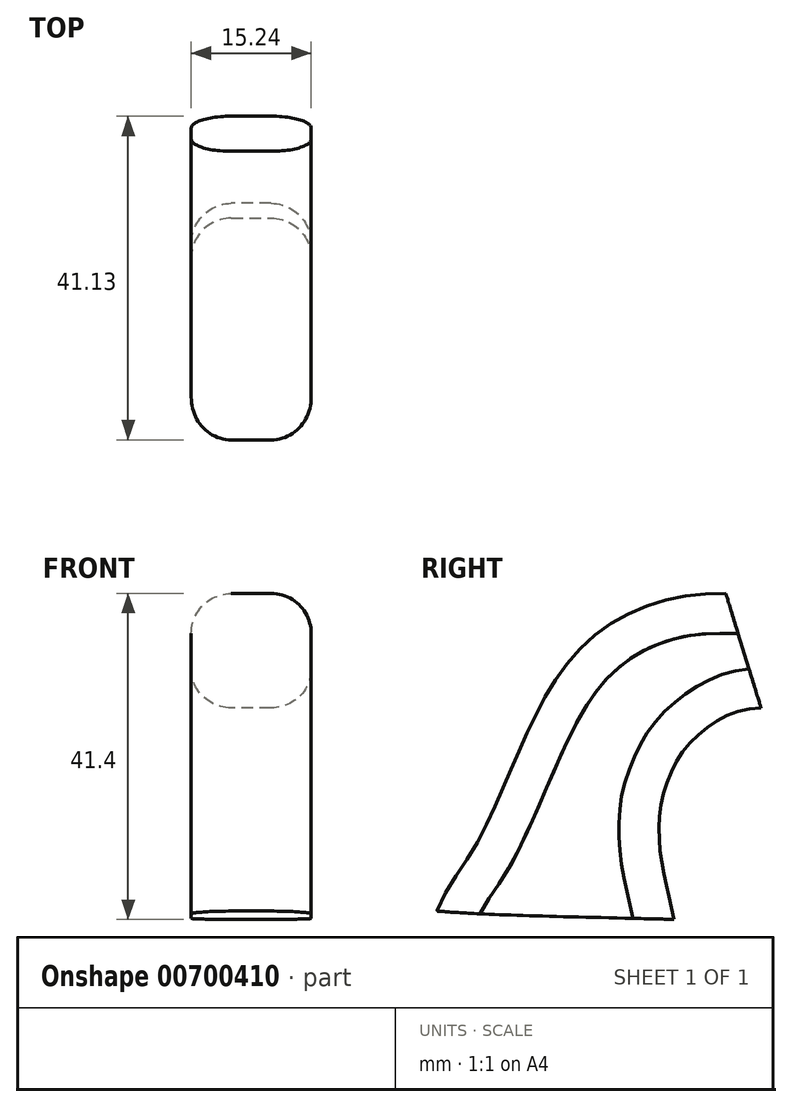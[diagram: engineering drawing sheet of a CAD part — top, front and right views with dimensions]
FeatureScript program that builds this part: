
annotation { "Feature Type Name" : "Feature", "Feature Type Description" : "" }
export const myFeature = defineFeature(function(context is Context, id is Id, definition is map)
    precondition{}
    {
        {
            var Q0;
            Q0=qCreatedBy(makeId("Right.planeOp"),FACE);
            var sketch = newSketch(context, id + "F0", { "sketchPlane" : qUnion([Q0])});
            skLineSegment(sketch, "E0", {"start": v(37.28, 25.36) * mm, "end": v(105.89, 25.36) * mm});
            skFitSpline(sketch, "E1", {"points": [v(-10.84, 4.07) * mm, v(-16.36, 3.73) * mm, v(-23.37, 1.43) * mm, v(-29.24, -2.83) * mm, v(-34.98, -11.33) * mm, v(-42.45, -27.65) * mm, v(-45.67, -32.6) * mm, v(-47.51, -36.27) * mm], "startDerivative": vector(-44.57, -0.2) * mm, "endDerivative": vector(-16.28, -36.6) * mm});
            skFitSpline(sketch, "E2", {"points": [v(-47.51, -36.27) * mm, v(-41.71, -36.64) * mm, v(-17.45, -37.32) * mm], "startDerivative": vector(14.62, -1.12) * mm, "endDerivative": vector(42.34, -0.99) * mm});
            skFitSpline(sketch, "E3", {"points": [v(-17.45, -37.32) * mm, v(-18.37, -32.95) * mm, v(-19.2, -28.6) * mm, v(-19.05, -22.42) * mm, v(-18, -19.24) * mm, v(-16.6, -16.4) * mm, v(-13.35, -13.06) * mm, v(-9.49, -10.97) * mm, v(-6.38, -10.46) * mm], "startDerivative": vector(-7.02, 34.52) * mm, "endDerivative": vector(28.1, 2.44) * mm});
            skFitSpline(sketch, "E4", {"points": [v(-6.38, -10.46) * mm, v(-4.63, -10.94) * mm, v(-1.93, -13.85) * mm, v(-0.46, -16.1) * mm, v(1.21, -18.15) * mm, v(3.1, -19.07) * mm, v(5.62, -19.52) * mm, v(11.6, -18.94) * mm, v(16.52, -16.72) * mm, v(17.44, -15.66) * mm, v(18.02, -13.37) * mm, v(18.06, -8.62) * mm, v(19.53, -6.67) * mm, v(20.55, -5.4) * mm], "startDerivative": vector(27.77, -2.36) * mm, "endDerivative": vector(15.83, 21.94) * mm});
            skLineSegment(sketch, "E5", {"start": v(-10.84, 4.07) * mm, "end": v(-6.38, -10.46) * mm});
            skSolve(sketch);
        }
        {
            var Q0;
            Q0=makeQuery(id+"F0.imprint","IMPRINT",FACE,{"disambiguationData":[TD([[makeQuery(id+"F0.imprint","IMPRINT",EDGE,{"derivedFrom":sQuery(id+"F0.wireOp",EDGE,"E1")}),1.0]])]});
            extrude(context, id + "F1", {"entities" : qUnion([Q0]), "depth" : 7.62 * mm, "offsetDistance" : 25.4 * mm});
        }
        {
            var Q0;
            Q0=makeQuery(id+"F0.imprint","IMPRINT",FACE,{"disambiguationData":[TD([[makeQuery(id+"F0.imprint","IMPRINT",EDGE,{"derivedFrom":sQuery(id+"F0.wireOp",EDGE,"E1")}),1.0]])]});
            extrude(context, id + "F2", {"entities" : qUnion([Q0]), "operationType" : NewBodyOperationType.ADD, "oppositeDirection" : true, "depth" : 7.62 * mm, "offsetDistance" : 25.4 * mm});
        }
        {
            var Q0;
            Q0=makeQuery(id+"F2.opExtrude","CAP_EDGE",EDGE,{"disambiguationData":[OSD([sQuery(id+"F0.wireOp",EDGE,"E1")])],"isStart":false});
            var Q1;
            Q1=makeQuery(id+"F2.opExtrude","CAP_EDGE",EDGE,{"disambiguationData":[OSD([sQuery(id+"F0.wireOp",EDGE,"E3")])],"isStart":false});
            var Q2;
            Q2=makeQuery(id+"F1.opExtrude","CAP_EDGE",EDGE,{"disambiguationData":[OSD([sQuery(id+"F0.wireOp",EDGE,"E1")])],"isStart":false});
            var Q3;
            Q3=makeQuery(id+"F1.opExtrude","CAP_EDGE",EDGE,{"disambiguationData":[OSD([sQuery(id+"F0.wireOp",EDGE,"E3")])],"isStart":false});
            fillet(context, id + "F3", {"entities" : qUnion([Q0, Q1, Q2, Q3]), "radius" : 5.08 * mm, "tangentPropagation" : true, "allowEdgeOverflow" : false});
        }
    });
